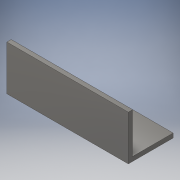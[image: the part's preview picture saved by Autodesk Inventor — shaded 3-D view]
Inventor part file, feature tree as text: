
AUTODESK INVENTOR PART (.ipt)
format: ipt  version: 2017 (Build 210142000, 142)  size: 102,400 bytes
history: native  units: in
note: dims shown in document units (in); Inventor stores cm internally (conversion verified against a paired STEP export)
features: extrude x2, sketch x2
ambient origin geometry x8: Origin, YZ Plane, XZ Plane, XY Plane, X Axis, Y Axis, Z Axis, Center Point
bodies: Solid1 (feature_tree)
feature tree (4):
  extrude  "Extrusion1"  Depth=4.2in
  extrude  "Extrusion2"  Depth=0.15in TaperAngle=0.0deg
  sketch  "Sketch1"  dims[d0=1.4in d1=4.2in]
  sketch  "Sketch2"  dims[d2=0.15in d3=0.15in d4=0.0in d5=1.4in d6=0.0in]
